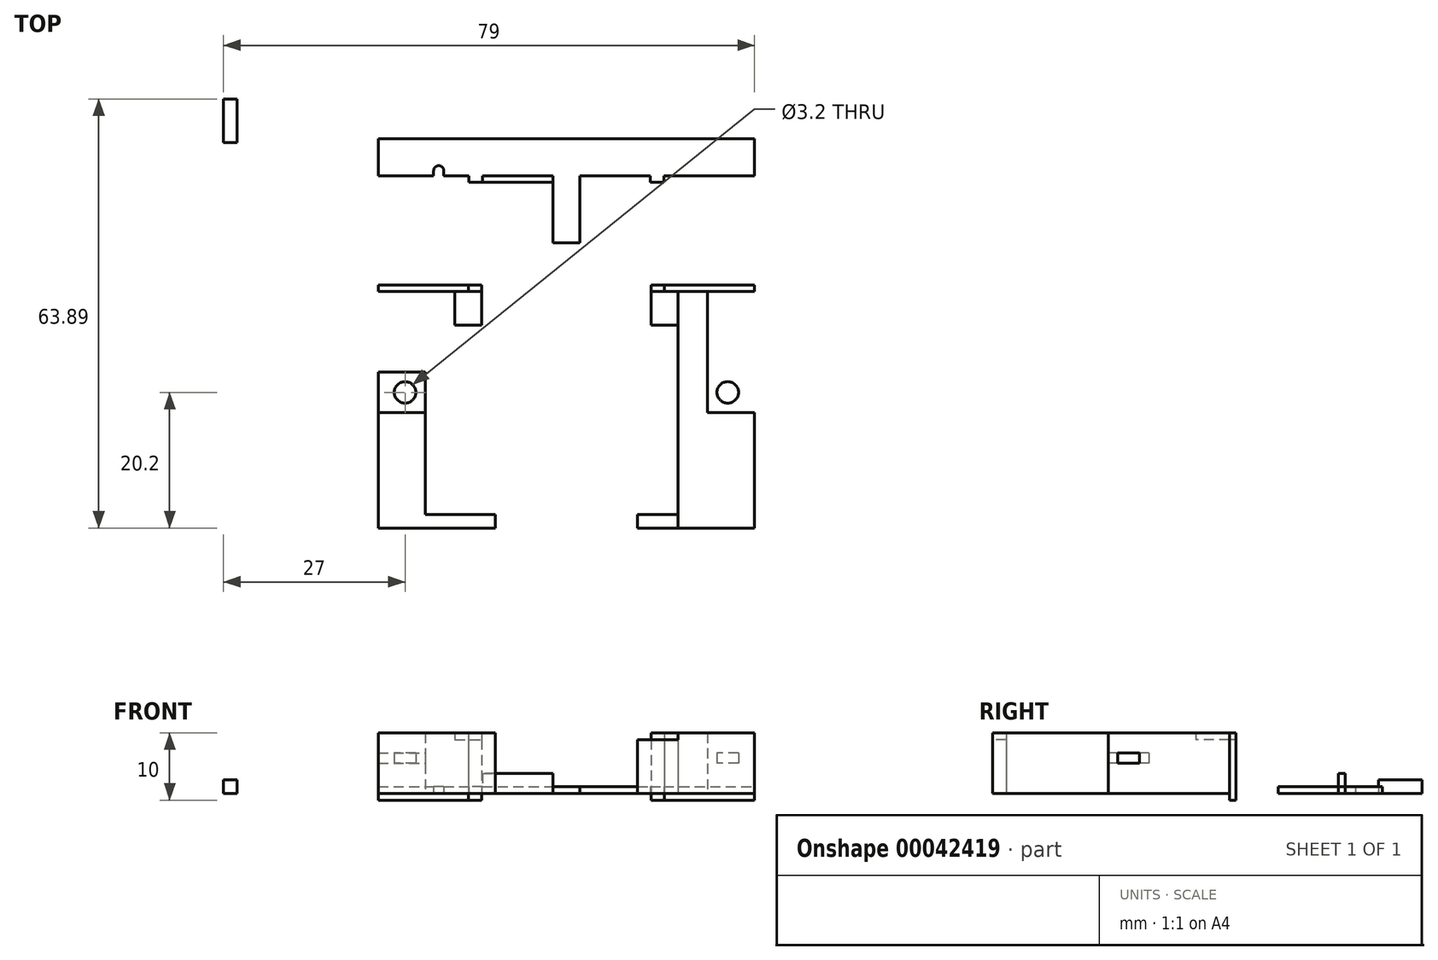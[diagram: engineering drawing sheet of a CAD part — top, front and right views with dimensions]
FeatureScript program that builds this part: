
annotation { "Feature Type Name" : "Feature", "Feature Type Description" : "" }
export const myFeature = defineFeature(function(context is Context, id is Id, definition is map)
    precondition{}
    {
        {
            var Q0;
            Q0=qCreatedBy(makeId("Top.planeOp"),FACE);
            var sketch = newSketch(context, id + "F0", { "sketchPlane" : qUnion([Q0])});
            skCircle(sketch, "E0", {"center": v(-24, 0) * mm, "radius": 1.6 * mm});
            skCircle(sketch, "E1", {"center": v(-24, 0) * mm, "radius": 3 * mm});
            skLineSegment(sketch, "E2.bottom", {"start": v(-21, 3) * mm, "end": v(-28, 3) * mm});
            skLineSegment(sketch, "E2.top", {"start": v(-21, -20.2) * mm, "end": v(-28, -20.2) * mm});
            skLineSegment(sketch, "E2.left", {"start": v(-21, 3) * mm, "end": v(-21, -20.2) * mm});
            skLineSegment(sketch, "E2.right", {"start": v(-28, 3) * mm, "end": v(-28, -20.2) * mm});
            skLineSegment(sketch, "E3", {"start": v(-28, -3) * mm, "end": v(-21, -3) * mm});
            skLineSegment(sketch, "E4.bottom", {"start": v(-16.6, 15) * mm, "end": v(-21, 15) * mm});
            skLineSegment(sketch, "E4.top", {"start": v(-16.6, -18.2) * mm, "end": v(-21, -18.2) * mm});
            skLineSegment(sketch, "E4.left", {"start": v(-16.6, 15) * mm, "end": v(-16.6, -18.2) * mm});
            skLineSegment(sketch, "E4.right", {"start": v(-21, 15) * mm, "end": v(-21, -18.2) * mm});
            skLineSegment(sketch, "E5.bottom", {"start": v(-21, -18.2) * mm, "end": v(-10.6, -18.2) * mm});
            skLineSegment(sketch, "E5.top", {"start": v(-21, -20.2) * mm, "end": v(-10.6, -20.2) * mm});
            skLineSegment(sketch, "E5.left", {"start": v(-21, -18.2) * mm, "end": v(-21, -20.2) * mm});
            skLineSegment(sketch, "E5.right", {"start": v(-10.6, -18.2) * mm, "end": v(-10.6, -20.2) * mm});
            skLineSegment(sketch, "E6.bottom", {"start": v(-16.6, 15) * mm, "end": v(-12.6, 15) * mm});
            skLineSegment(sketch, "E6.top", {"start": v(-16.6, 10) * mm, "end": v(-12.6, 10) * mm});
            skLineSegment(sketch, "E6.left", {"start": v(-16.6, 15) * mm, "end": v(-16.6, 10) * mm});
            skLineSegment(sketch, "E6.right", {"start": v(-12.6, 15) * mm, "end": v(-12.6, 10) * mm});
            skLineSegment(sketch, "E7.bottom", {"start": v(-16.6, -18.2) * mm, "end": v(-12.6, -18.2) * mm});
            skLineSegment(sketch, "E7.top", {"start": v(-16.6, -13.2) * mm, "end": v(-12.6, -13.2) * mm});
            skLineSegment(sketch, "E7.left", {"start": v(-16.6, -18.2) * mm, "end": v(-16.6, -13.2) * mm});
            skLineSegment(sketch, "E7.right", {"start": v(-12.6, -18.2) * mm, "end": v(-12.6, -13.2) * mm});
            skLineSegment(sketch, "E8.bottom", {"start": v(-12.6, 15) * mm, "end": v(-28, 15) * mm});
            skLineSegment(sketch, "E8.top", {"start": v(-12.6, 16) * mm, "end": v(-28, 16) * mm});
            skLineSegment(sketch, "E8.left", {"start": v(-12.6, 15) * mm, "end": v(-12.6, 16) * mm});
            skLineSegment(sketch, "E8.right", {"start": v(-28, 15) * mm, "end": v(-28, 16) * mm});
            skLineSegment(sketch, "E9.rect.bottom", {"start": v(-17.6, -9.1) * mm, "end": v(-16.6, -9.1) * mm});
            skLineSegment(sketch, "E9.rect.top", {"start": v(-17.6, 5.9) * mm, "end": v(-16.6, 5.9) * mm});
            skLineSegment(sketch, "E9.rect.left", {"start": v(-17.6, -9.1) * mm, "end": v(-17.6, 5.9) * mm});
            skLineSegment(sketch, "E9.rect.right", {"start": v(-16.6, -9.1) * mm, "end": v(-16.6, 5.9) * mm});
            skPoint(sketch, "E9.rect.middle", {"position": v(-17.1, -1.6) * mm});
            skLineSegment(sketch, "E10.MirrorCS", {"start": v(28, 3) * mm, "end": v(28, -20.2) * mm});
            skLineSegment(sketch, "E11.MirrorCS", {"start": v(21, 15) * mm, "end": v(21, -18.2) * mm});
            skLineSegment(sketch, "E12.MirrorCS", {"start": v(21, 3) * mm, "end": v(21, -20.2) * mm});
            skLineSegment(sketch, "E13.MirrorCS", {"start": v(10.6, -18.2) * mm, "end": v(10.6, -20.2) * mm});
            skLineSegment(sketch, "E14.MirrorCS", {"start": v(16.6, -18.2) * mm, "end": v(16.6, -13.2) * mm});
            skLineSegment(sketch, "E15.MirrorCS", {"start": v(16.6, 15) * mm, "end": v(16.6, -18.2) * mm});
            skLineSegment(sketch, "E16.MirrorCS", {"start": v(12.6, 15) * mm, "end": v(12.6, 10) * mm});
            skLineSegment(sketch, "E17.MirrorCS", {"start": v(28, 15) * mm, "end": v(28, 16) * mm});
            skLineSegment(sketch, "E18.MirrorCS", {"start": v(12.6, 15) * mm, "end": v(12.6, 16) * mm});
            skLineSegment(sketch, "E19.MirrorCS", {"start": v(12.6, 16) * mm, "end": v(28, 16) * mm});
            skLineSegment(sketch, "E20.MirrorCS", {"start": v(12.6, 15) * mm, "end": v(28, 15) * mm});
            skLineSegment(sketch, "E21.MirrorCS", {"start": v(16.6, 10) * mm, "end": v(12.6, 10) * mm});
            skLineSegment(sketch, "E22.MirrorCS", {"start": v(21, -18.2) * mm, "end": v(10.6, -18.2) * mm});
            skLineSegment(sketch, "E23.MirrorCS", {"start": v(21, -20.2) * mm, "end": v(10.6, -20.2) * mm});
            skLineSegment(sketch, "E24.MirrorCS", {"start": v(21, -20.2) * mm, "end": v(28, -20.2) * mm});
            skLineSegment(sketch, "E25.MirrorCS", {"start": v(28, -3) * mm, "end": v(21, -3) * mm});
            skCircle(sketch, "E26.MirrorC", {"center": v(24, 0) * mm, "radius": 1.6 * mm});
            skLineSegment(sketch, "E27", {"start": v(-14.6, 16) * mm, "end": v(-14.6, 15) * mm});
            skLineSegment(sketch, "E28.MirrorCS", {"start": v(14.6, 16) * mm, "end": v(14.6, 15) * mm});
            skLineSegment(sketch, "E29.MirrorCS", {"start": v(21, 3) * mm, "end": v(28, 3) * mm});
            skLineSegment(sketch, "E30", {"start": v(16.6, -18.2) * mm, "end": v(16.6, -20.2) * mm});
            skSolve(sketch);
        }
        {
            var Q0;
            {var subQ13=sQuery(id+"F0.wireOp",EDGE,"E6.left");Q0=makeQuery(id+"F0.imprint","IMPRINT",FACE,{"disambiguationData":[TD([[makeQuery(id+"F0.imprint","IMPRINT",EDGE,{"derivedFrom":subQ13}),-1.0]])]});}
            var Q1;
            {var subQ3=sQuery(id+"F0.wireOp",EDGE,"E11.MirrorCS");Q1=makeQuery(id+"F0.imprint","IMPRINT",FACE,{"disambiguationData":[TD([[makeQuery(id+"F0.imprint","IMPRINT",EDGE,{"derivedFrom":subQ3}),-1.0]])]});}
            var Q2;
            Q2=makeQuery(id+"F0.imprint","IMPRINT",FACE,{"disambiguationData":[TD([[makeQuery(id+"F0.imprint","IMPRINT",EDGE,{"derivedFrom":sQuery(id+"F0.wireOp",EDGE,"E5.top")}),1.0]])]});
            var Q3;
            {var subQ4=sQuery(id+"F0.wireOp",EDGE,"E2.top");Q3=makeQuery(id+"F0.imprint","IMPRINT",FACE,{"disambiguationData":[TD([[makeQuery(id+"F0.imprint","IMPRINT",EDGE,{"derivedFrom":subQ4}),-1.0]])]});}
            var Q4;
            {var subQ0=sQuery(id+"F0.wireOp",EDGE,"E25.MirrorCS");Q4=makeQuery(id+"F0.imprint","IMPRINT",FACE,{"disambiguationData":[TD([[makeQuery(id+"F0.imprint","IMPRINT",EDGE,{"derivedFrom":subQ0}),1.0]])]});}
            var Q5;
            {var subQ0=sQuery(id+"F0.wireOp",EDGE,"E30");Q5=makeQuery(id+"F0.imprint","IMPRINT",FACE,{"disambiguationData":[TD([[makeQuery(id+"F0.imprint","IMPRINT",EDGE,{"derivedFrom":subQ0}),1.0]])]});}
            extrude(context, id + "F1", {"entities" : qUnion([Q0, Q1, Q2, Q3, Q4, Q5]), "depth" : 9 * mm});
        }
        {
            var Q0;
            Q0=makeQuery(id+"F0.imprint","IMPRINT",FACE,{"disambiguationData":[TD([[makeQuery(id+"F0.imprint","IMPRINT",EDGE,{"derivedFrom":sQuery(id+"F0.wireOp",EDGE,"E6.top")}),1.0]])]});
            var Q1;
            Q1=makeQuery(id+"F0.imprint","IMPRINT",FACE,{"disambiguationData":[TD([[makeQuery(id+"F0.imprint","IMPRINT",EDGE,{"derivedFrom":sQuery(id+"F0.wireOp",EDGE,"E7.bottom")}),1.0]])]});
            var Q2;
            {var subQ2=sQuery(id+"F0.wireOp",EDGE,"E16.MirrorCS");Q2=makeQuery(id+"F0.imprint","IMPRINT",FACE,{"disambiguationData":[TD([[makeQuery(id+"F0.imprint","IMPRINT",EDGE,{"derivedFrom":subQ2}),1.0]])]});}
            extrude(context, id + "F2", {"entities" : qUnion([Q0, Q1, Q2]), "depth" : 9 * mm, "hasSecondDirection" : true, "secondDirectionOppositeDirection" : false, "secondDirectionDepth" : 8 * mm});
        }
        {
            var Q0;
            {var subQ1=sQuery(id+"F0.wireOp",EDGE,"E1");var subQ5=sQuery(id+"F0.wireOp",EDGE,"E2.bottom");var subQ7=makeQuery(id+"F0.imprint","INTERSECT",VERTEX,{"derivedFrom":[subQ1,subQ5]});Q0=makeQuery(id+"F0.imprint","IMPRINT",FACE,{"disambiguationData":[TD([[makeQuery(id+"F0.imprint","IMPRINT",EDGE,{"disambiguationData":[TD([[subQ7,-1.0]])],"derivedFrom":subQ1}),-1.0]])]});}
            var Q1;
            Q1=makeQuery(id+"F0.imprint","IMPRINT",FACE,{"disambiguationData":[TD([[makeQuery(id+"F0.imprint","IMPRINT",EDGE,{"derivedFrom":sQuery(id+"F0.wireOp",EDGE,"E0")}),-1.0]])]});
            var Q2;
            {var subQ1=sQuery(id+"F0.wireOp",EDGE,"E1");var subQ3=sQuery(id+"F0.wireOp",EDGE,"E2.bottom");var subQ5=makeQuery(id+"F0.imprint","INTERSECT",VERTEX,{"derivedFrom":[subQ1,subQ3]});Q2=makeQuery(id+"F0.imprint","IMPRINT",FACE,{"disambiguationData":[TD([[makeQuery(id+"F0.imprint","IMPRINT",EDGE,{"disambiguationData":[TD([[subQ5,1.0]])],"derivedFrom":subQ1}),-1.0]])]});}
            var Q3;
            {var subQ0=sQuery(id+"F0.wireOp",EDGE,"E4.right");var subQ1=sQuery(id+"F0.wireOp",EDGE,"E1");var subQ2=makeQuery(id+"F0.imprint","INTERSECT",VERTEX,{"derivedFrom":[subQ1,subQ0]});Q3=makeQuery(id+"F0.imprint","IMPRINT",FACE,{"disambiguationData":[TD([[makeQuery(id+"F0.imprint","IMPRINT",EDGE,{"disambiguationData":[TD([[subQ2,1.0]])],"derivedFrom":subQ1}),-1.0]])]});}
            var Q4;
            Q4=makeQuery(id+"F0.imprint","IMPRINT",FACE,{"disambiguationData":[TD([[makeQuery(id+"F0.imprint","IMPRINT",EDGE,{"derivedFrom":sQuery(id+"F0.wireOp",EDGE,"E26.MirrorC")}),1.0]])]});
            extrude(context, id + "F3", {"entities" : qUnion([Q0, Q1, Q2, Q3, Q4]), "depth" : 6 * mm, "hasSecondDirection" : true, "secondDirectionOppositeDirection" : false, "secondDirectionDepth" : 4.5 * mm});
        }
        {
            var Q0;
            {var subQ1=sQuery(id+"F0.wireOp",EDGE,"E8.right");Q0=makeQuery(id+"F0.imprint","IMPRINT",FACE,{"disambiguationData":[TD([[makeQuery(id+"F0.imprint","IMPRINT",EDGE,{"derivedFrom":subQ1}),-1.0]])]});}
            var Q1;
            {var subQ1=sQuery(id+"F0.wireOp",EDGE,"E17.MirrorCS");Q1=makeQuery(id+"F0.imprint","IMPRINT",FACE,{"disambiguationData":[TD([[makeQuery(id+"F0.imprint","IMPRINT",EDGE,{"derivedFrom":subQ1}),1.0]])]});}
            extrude(context, id + "F4", {"entities" : qUnion([Q0, Q1]), "depth" : 9 * mm, "hasSecondDirection" : true, "secondDirectionOppositeDirection" : true, "secondDirectionDepth" : 1 * mm});
        }
        {
            var Q0;
            {var subQ1=sQuery(id+"F0.wireOp",EDGE,"E8.left");Q0=makeQuery(id+"F0.imprint","IMPRINT",FACE,{"disambiguationData":[TD([[makeQuery(id+"F0.imprint","IMPRINT",EDGE,{"derivedFrom":subQ1}),1.0]])]});}
            var Q1;
            {var subQ2=sQuery(id+"F0.wireOp",EDGE,"E18.MirrorCS");Q1=makeQuery(id+"F0.imprint","IMPRINT",FACE,{"disambiguationData":[TD([[makeQuery(id+"F0.imprint","IMPRINT",EDGE,{"derivedFrom":subQ2}),-1.0]])]});}
            extrude(context, id + "F5", {"entities" : qUnion([Q0, Q1]), "depth" : 8 * mm, "hasSecondDirection" : true, "secondDirectionOppositeDirection" : true, "secondDirectionDepth" : 1 * mm});
        }
        {
            var Q0;
            Q0=qCreatedBy(makeId("Top.planeOp"),FACE);
            var sketch = newSketch(context, id + "F6", { "sketchPlane" : qUnion([Q0])});
            skLineSegment(sketch, "E31.rect.bottom", {"start": v(-28, 32.25) * mm, "end": v(-19.75, 32.25) * mm});
            skLineSegment(sketch, "E31.rect.top", {"start": v(-28, 37.75) * mm, "end": v(28, 37.75) * mm});
            skLineSegment(sketch, "E31.rect.left", {"start": v(-28, 32.25) * mm, "end": v(-28, 37.75) * mm});
            skLineSegment(sketch, "E31.rect.right", {"start": v(28, 32.25) * mm, "end": v(28, 37.75) * mm});
            skPoint(sketch, "E31.rect.middle", {"position": v(0, 35) * mm});
            skLineSegment(sketch, "E32.bottom", {"start": v(-2, 32.25) * mm, "end": v(2, 32.25) * mm});
            skLineSegment(sketch, "E32.top", {"start": v(-2, 22.25) * mm, "end": v(2, 22.25) * mm});
            skLineSegment(sketch, "E32.left", {"start": v(-2, 32.25) * mm, "end": v(-2, 22.25) * mm});
            skLineSegment(sketch, "E32.right", {"start": v(2, 32.25) * mm, "end": v(2, 22.25) * mm});
            skLineSegment(sketch, "E33.bottom", {"start": v(2, 32.25) * mm, "end": v(14.5, 32.25) * mm});
            skLineSegment(sketch, "E33.top", {"start": v(2, 31.25) * mm, "end": v(14.5, 31.25) * mm});
            skLineSegment(sketch, "E33.left", {"start": v(2, 32.25) * mm, "end": v(2, 31.25) * mm});
            skLineSegment(sketch, "E33.right", {"start": v(14.5, 32.25) * mm, "end": v(14.5, 31.25) * mm});
            skLineSegment(sketch, "E34", {"start": v(12.5, 32.25) * mm, "end": v(12.5, 31.25) * mm});
            skLineSegment(sketch, "E35.MirrorCS", {"start": v(-2, 31.25) * mm, "end": v(-14.5, 31.25) * mm});
            skLineSegment(sketch, "E36.MirrorCS", {"start": v(-12.5, 32.25) * mm, "end": v(-12.5, 31.25) * mm});
            skLineSegment(sketch, "E37.MirrorCS", {"start": v(-14.5, 32.25) * mm, "end": v(-14.5, 31.25) * mm});
            skArc(sketch, "E38", {"start": v(-18.25, 33) * mm, "mid": v(-19, 33.75) * mm, "end": v(-19.75, 33) * mm});
            skLineSegment(sketch, "E39", {"start": v(-18.25, 33) * mm, "end": v(-18.25, 32.25) * mm});
            skLineSegment(sketch, "E40", {"start": v(-19.75, 32.25) * mm, "end": v(-19.75, 33) * mm});
            skLineSegment(sketch, "E41.trimOffspring", {"start": v(-18.25, 32.25) * mm, "end": v(28, 32.25) * mm});
            skSolve(sketch);
        }
        {
            var Q0;
            Q0=makeQuery(id+"F6.imprint","IMPRINT",FACE,{"disambiguationData":[TD([[makeQuery(id+"F6.imprint","IMPRINT",EDGE,{"derivedFrom":sQuery(id+"F6.wireOp",EDGE,"E31.rect.bottom")}),1.0]])]});
            var Q1;
            {var subQ2=sQuery(id+"F6.wireOp",EDGE,"E36.MirrorCS");Q1=makeQuery(id+"F6.imprint","IMPRINT",FACE,{"disambiguationData":[TD([[makeQuery(id+"F6.imprint","IMPRINT",EDGE,{"derivedFrom":subQ2}),-1.0]])]});}
            var Q2;
            {var subQ2=sQuery(id+"F6.wireOp",EDGE,"E33.right");Q2=makeQuery(id+"F6.imprint","IMPRINT",FACE,{"disambiguationData":[TD([[makeQuery(id+"F6.imprint","IMPRINT",EDGE,{"derivedFrom":subQ2}),-1.0]])]});}
            var Q3;
            {var subQ4=sQuery(id+"F6.wireOp",EDGE,"E32.top");Q3=makeQuery(id+"F6.imprint","IMPRINT",FACE,{"disambiguationData":[TD([[makeQuery(id+"F6.imprint","IMPRINT",EDGE,{"derivedFrom":subQ4}),1.0]])]});}
            extrude(context, id + "F7", {"entities" : qUnion([Q0, Q1, Q2, Q3]), "depth" : 1 * mm});
        }
        {
            var Q0;
            {var subQ0=sQuery(id+"F6.wireOp",EDGE,"E36.MirrorCS");Q0=makeQuery(id+"F6.imprint","IMPRINT",FACE,{"disambiguationData":[TD([[makeQuery(id+"F6.imprint","IMPRINT",EDGE,{"derivedFrom":subQ0}),1.0]])]});}
            var Q1;
            {var subQ2=sQuery(id+"F6.wireOp",EDGE,"E33.left");Q1=makeQuery(id+"F6.imprint","IMPRINT",FACE,{"disambiguationData":[TD([[makeQuery(id+"F6.imprint","IMPRINT",EDGE,{"derivedFrom":subQ2}),1.0]])]});}
            extrude(context, id + "F8", {"entities" : qUnion([Q0, Q1]), "operationType" : NewBodyOperationType.ADD, "depth" : 3 * mm});
        }
        {
            var Q0;
            Q0=qCreatedBy(makeId("Top.planeOp"),FACE);
            var sketch = newSketch(context, id + "F9", { "sketchPlane" : qUnion([Q0])});
            skLineSegment(sketch, "E42.bottom", {"start": v(-51, 43.69) * mm, "end": v(-49, 43.69) * mm});
            skLineSegment(sketch, "E42.top", {"start": v(-51, 37.19) * mm, "end": v(-49, 37.19) * mm});
            skLineSegment(sketch, "E42.left", {"start": v(-51, 43.69) * mm, "end": v(-51, 37.19) * mm});
            skLineSegment(sketch, "E42.right", {"start": v(-49, 43.69) * mm, "end": v(-49, 37.19) * mm});
            skSolve(sketch);
        }
        {
            var Q0;
            Q0=makeQuery(id+"F9.imprint","IMPRINT",FACE,{"disambiguationData":[TD([[makeQuery(id+"F9.imprint","IMPRINT",EDGE,{"derivedFrom":sQuery(id+"F9.wireOp",EDGE,"E42.bottom")}),-1.0]])]});
            extrude(context, id + "F10", {"entities" : qUnion([Q0]), "depth" : 2 * mm});
        }
        {
            var Q0;
            {var subQ2=sQuery(id+"F0.wireOp",EDGE,"E13.MirrorCS");Q0=makeQuery(id+"F0.imprint","IMPRINT",FACE,{"disambiguationData":[TD([[makeQuery(id+"F0.imprint","IMPRINT",EDGE,{"derivedFrom":subQ2}),1.0]])]});}
            extrude(context, id + "F11", {"entities" : qUnion([Q0]), "operationType" : NewBodyOperationType.ADD, "depth" : 8 * mm});
        }
    });
